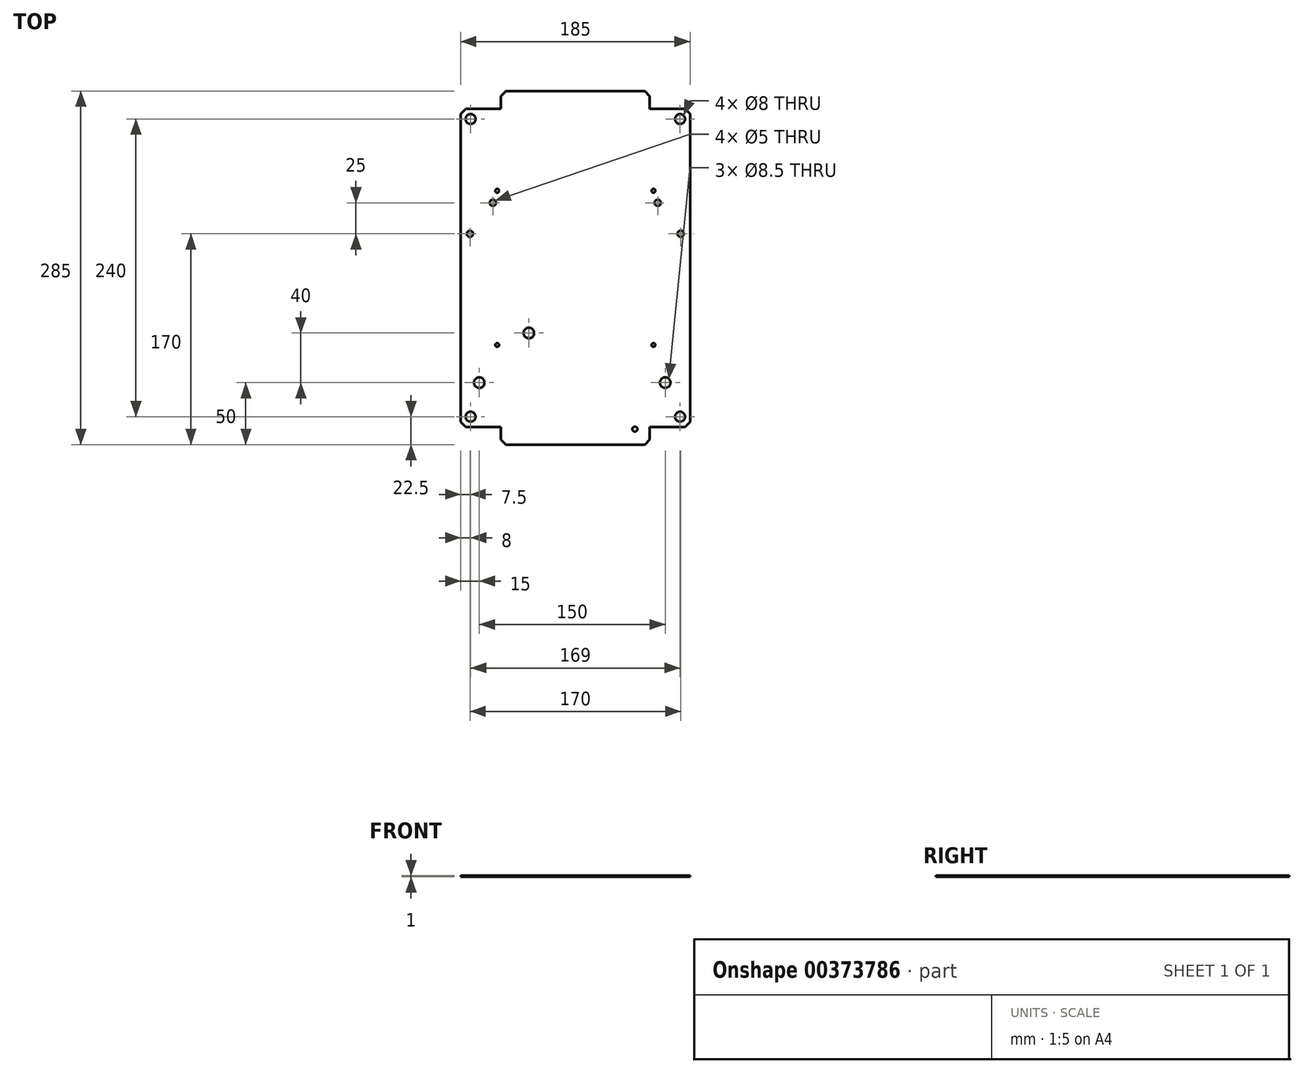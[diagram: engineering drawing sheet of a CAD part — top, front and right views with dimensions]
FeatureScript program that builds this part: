
annotation { "Feature Type Name" : "Feature", "Feature Type Description" : "" }
export const myFeature = defineFeature(function(context is Context, id is Id, definition is map)
    precondition{}
    {
        {
            var Q0;
            Q0=qCreatedBy(makeId("Top.planeOp"),FACE);
            var sketch = newSketch(context, id + "F0", { "sketchPlane" : qUnion([Q0])});
            skLineSegment(sketch, "E0", {"start": v(-92.5, 0) * mm, "end": v(-92.5, 128.2) * mm});
            skLineSegment(sketch, "E1", {"start": v(-92.5, 128.2) * mm, "end": v(-60, 128.2) * mm});
            skLineSegment(sketch, "E2", {"start": v(-60, 128.2) * mm, "end": v(-60, 142.5) * mm});
            skLineSegment(sketch, "E3", {"start": v(-60, 142.5) * mm, "end": v(0, 142.5) * mm});
            skCircle(sketch, "E4", {"center": v(-84.5, 120) * mm, "radius": 4 * mm});
            skCircle(sketch, "E5.MirrorC", {"center": v(84.5, 120) * mm, "radius": 4 * mm});
            skLineSegment(sketch, "E6.MirrorCS", {"start": v(60, 128.2) * mm, "end": v(60, 142.5) * mm});
            skLineSegment(sketch, "E7.MirrorCS", {"start": v(60, 142.5) * mm, "end": v(0, 142.5) * mm});
            skLineSegment(sketch, "E8.MirrorCS", {"start": v(92.5, 0) * mm, "end": v(92.5, 128.2) * mm});
            skLineSegment(sketch, "E9.MirrorCS", {"start": v(92.5, 128.2) * mm, "end": v(60, 128.2) * mm});
            skCircle(sketch, "E10.MirrorC", {"center": v(84.5, -120) * mm, "radius": 4 * mm});
            skCircle(sketch, "E11.MirrorC", {"center": v(-84.5, -120) * mm, "radius": 4 * mm});
            skLineSegment(sketch, "E12.MirrorCS", {"start": v(-60, -142.5) * mm, "end": v(0, -142.5) * mm});
            skLineSegment(sketch, "E13.MirrorCS", {"start": v(-60, -128.2) * mm, "end": v(-60, -142.5) * mm});
            skLineSegment(sketch, "E14.MirrorCS", {"start": v(-92.5, 0) * mm, "end": v(-92.5, -128.2) * mm});
            skLineSegment(sketch, "E15.MirrorCS", {"start": v(-92.5, -128.2) * mm, "end": v(-60, -128.2) * mm});
            skLineSegment(sketch, "E16.MirrorCS", {"start": v(60, -128.2) * mm, "end": v(60, -142.5) * mm});
            skLineSegment(sketch, "E17.MirrorCS", {"start": v(60, -142.5) * mm, "end": v(0, -142.5) * mm});
            skLineSegment(sketch, "E18.MirrorCS", {"start": v(92.5, -128.2) * mm, "end": v(60, -128.2) * mm});
            skLineSegment(sketch, "E19.MirrorCS", {"start": v(92.5, 0) * mm, "end": v(92.5, -128.2) * mm});
            skCircle(sketch, "E20", {"center": v(48, -130) * mm, "radius": 2 * mm});
            skCircle(sketch, "E21", {"center": v(-63, 62.2) * mm, "radius": 1.5 * mm});
            skCircle(sketch, "E22.MirrorC", {"center": v(63, 62.2) * mm, "radius": 1.5 * mm});
            skCircle(sketch, "E23.MirrorC", {"center": v(-63, -62.2) * mm, "radius": 1.5 * mm});
            skCircle(sketch, "E24.MirrorC", {"center": v(63, -62.2) * mm, "radius": 1.5 * mm});
            skCircle(sketch, "E25", {"center": v(-77.5, -92.5) * mm, "radius": 4.25 * mm});
            skCircle(sketch, "E26", {"center": v(-37.5, -52.5) * mm, "radius": 4.25 * mm});
            skCircle(sketch, "E27", {"center": v(72.5, -92.5) * mm, "radius": 4.25 * mm});
            skCircle(sketch, "E28", {"center": v(-85, 27.5) * mm, "radius": 2.5 * mm});
            skCircle(sketch, "E29", {"center": v(-66.5, 52.5) * mm, "radius": 2.5 * mm});
            skCircle(sketch, "E30.MirrorC", {"center": v(85, 27.5) * mm, "radius": 2.5 * mm});
            skCircle(sketch, "E31.MirrorC", {"center": v(66.5, 52.5) * mm, "radius": 2.5 * mm});
            skSolve(sketch);
        }
        {
            var Q0;
            Q0=qSketchRegion(id+"F0",true);
            extrude(context, id + "F1", {"entities" : qUnion([Q0]), "endBound" : BoundingType.SYMMETRIC, "depth" : 1 * mm});
        }
        {
            var Q0;
            Q0=makeQuery(id+"F1.opExtrude","SWEPT_EDGE",EDGE,{"disambiguationData":[OSD([sQuery(id+"F0.wireOp",EDGE,"E0"),sQuery(id+"F0.wireOp",EDGE,"E1")])]});
            var Q1;
            Q1=makeQuery(id+"F1.opExtrude","SWEPT_EDGE",EDGE,{"disambiguationData":[OSD([sQuery(id+"F0.wireOp",EDGE,"E2"),sQuery(id+"F0.wireOp",EDGE,"E3")])]});
            var Q2;
            Q2=makeQuery(id+"F1.opExtrude","SWEPT_EDGE",EDGE,{"disambiguationData":[OSD([sQuery(id+"F0.wireOp",EDGE,"E6.MirrorCS"),sQuery(id+"F0.wireOp",EDGE,"E7.MirrorCS")])]});
            var Q3;
            Q3=makeQuery(id+"F1.opExtrude","SWEPT_EDGE",EDGE,{"disambiguationData":[OSD([sQuery(id+"F0.wireOp",EDGE,"E8.MirrorCS"),sQuery(id+"F0.wireOp",EDGE,"E9.MirrorCS")])]});
            var Q4;
            Q4=makeQuery(id+"F1.opExtrude","SWEPT_EDGE",EDGE,{"disambiguationData":[OSD([sQuery(id+"F0.wireOp",EDGE,"E18.MirrorCS"),sQuery(id+"F0.wireOp",EDGE,"E19.MirrorCS")])]});
            var Q5;
            Q5=makeQuery(id+"F1.opExtrude","SWEPT_EDGE",EDGE,{"disambiguationData":[OSD([sQuery(id+"F0.wireOp",EDGE,"E16.MirrorCS"),sQuery(id+"F0.wireOp",EDGE,"E17.MirrorCS")])]});
            var Q6;
            Q6=makeQuery(id+"F1.opExtrude","SWEPT_EDGE",EDGE,{"disambiguationData":[OSD([sQuery(id+"F0.wireOp",EDGE,"E12.MirrorCS"),sQuery(id+"F0.wireOp",EDGE,"E13.MirrorCS")])]});
            var Q7;
            Q7=makeQuery(id+"F1.opExtrude","SWEPT_EDGE",EDGE,{"disambiguationData":[OSD([sQuery(id+"F0.wireOp",EDGE,"E14.MirrorCS"),sQuery(id+"F0.wireOp",EDGE,"E15.MirrorCS")])]});
            chamfer(context, id + "F2", {"entities" : qUnion([Q0, Q1, Q2, Q3, Q4, Q5, Q6, Q7]), "width" : 4 * mm, "tangentPropagation" : true});
        }
    });
